FCSTD DOCUMENT  (FreeCAD 0.17R13528 (Git))
Label: DataOutput
License: All rights reserved
LicenseURL: http://en.wikipedia.org/wiki/All_rights_reserved
objects: Spreadsheet::Sheet×1

FEATURE [Spreadsheet::Sheet] Spreadsheet
  cells = A1=Part Name; B1=Material; C1=Price per 1m2; D1=Square m2; E1=Total price; F1=Width, mm; G1=Height, mm; A2=GlassDarkFront; C2=900; D2==F2 * G2 / 1000000; E2==C2 * D2; F2==170 + 4 + 4; G2==40 + 4 + 210 + 4; A3=Mirror; C3=1150; D3==F3 * G3 / 1000000; E3==C3 * D3; F3=170; G3==210 + 4; A4=GlassDarkSide; C4=900; D4==F4 * G4 / 1000000; E4==C4 * D4; F4==50 + 4; G4=258; A5=GlassDarkSide; C5=900; D5==F5 * G5 / 1000000; E5==C5 * D5; F5==F4; G5==G4; A6=GlassDarkTop; C6=900; D6==F6 * G6 / 1000000; E6==C6 * D6; F6=170; G6=20; A7=GlassTransShelf; C7=520; D7==F7 * G7 / 1000000; E7==C7 * D7; F7=165; G7=50; A9=Total price for glass; B9==sum(E2:E7); A10=Total price for cutting; B10==40 * 6; A11=Total price for processing; B11==(sum(F2:F7) + sum(G2:G7)) * 2 / 1000 * 40; A12=Total for all; B12==sum(B9:B11)
